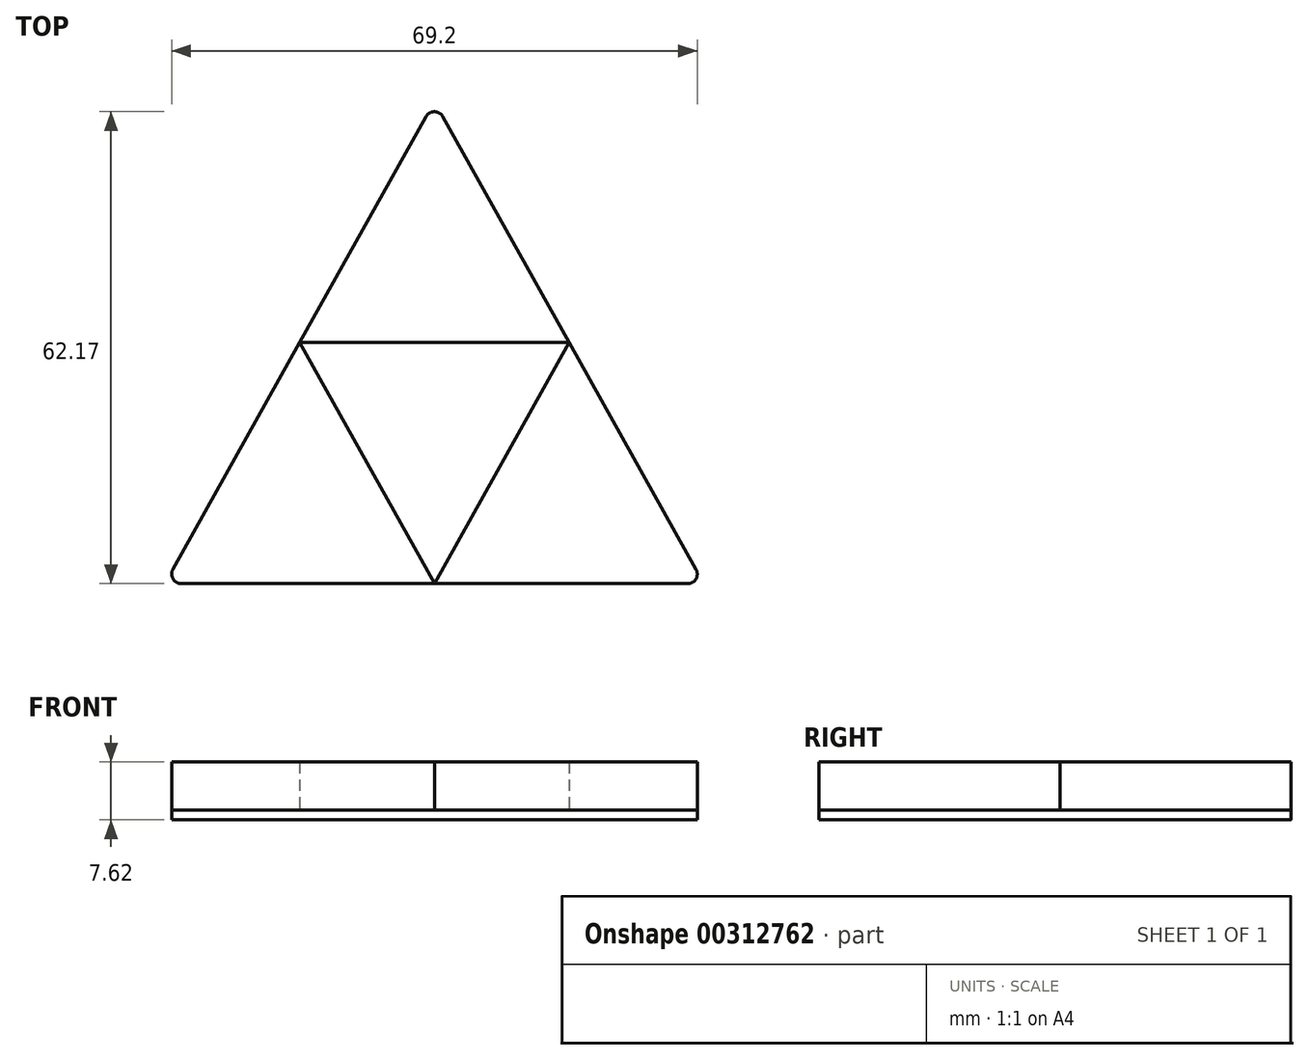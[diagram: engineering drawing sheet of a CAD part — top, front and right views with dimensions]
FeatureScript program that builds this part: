
annotation { "Feature Type Name" : "Feature", "Feature Type Description" : "" }
export const myFeature = defineFeature(function(context is Context, id is Id, definition is map)
    precondition{}
    {
        {
            var Q0;
            Q0=qCreatedBy(makeId("Top.planeOp"),FACE);
            var sketch = newSketch(context, id + "F0", { "sketchPlane" : qUnion([Q0])});
            skLineSegment(sketch, "E0.bottom", {"start": v(35.5, 31.75) * mm, "end": v(-35.5, 31.75) * mm});
            skLineSegment(sketch, "E0.top", {"start": v(35.5, -31.75) * mm, "end": v(-35.5, -31.75) * mm});
            skLineSegment(sketch, "E0.left", {"start": v(35.5, 31.75) * mm, "end": v(35.5, -31.75) * mm});
            skLineSegment(sketch, "E0.right", {"start": v(-35.5, 31.75) * mm, "end": v(-35.5, -31.75) * mm});
            skPoint(sketch, "E0.middle", {"position": v(0, 0) * mm});
            skLineSegment(sketch, "E1", {"start": v(0, 31.75) * mm, "end": v(-35.5, -31.75) * mm});
            skLineSegment(sketch, "E2", {"start": v(-35.5, -31.75) * mm, "end": v(35.5, -31.75) * mm});
            skLineSegment(sketch, "E3", {"start": v(35.5, -31.75) * mm, "end": v(0, 31.75) * mm});
            skSolve(sketch);
        }
        {
            var Q0;
            Q0=makeQuery(id+"F0.imprint","IMPRINT",FACE,{"disambiguationData":[TD([[makeQuery(id+"F0.imprint","IMPRINT",EDGE,{"derivedFrom":sQuery(id+"F0.wireOp",EDGE,"E1")}),1.0]])]});
            extrude(context, id + "F1", {"entities" : qUnion([Q0]), "depth" : 1.27 * mm});
        }
        {
            var Q0;
            Q0=makeQuery(id+"F1.opExtrude","CAP_FACE",FACE,{"disambiguationData":[OSD([sQuery(id+"F0.wireOp",EDGE,"E1"),sQuery(id+"F0.wireOp",EDGE,"E2"),sQuery(id+"F0.wireOp",EDGE,"E3")])],"isStart":false});
            var sketch = newSketch(context, id + "F2", { "sketchPlane" : qUnion([Q0])});
            skLineSegment(sketch, "E4", {"start": v(0, -31.75) * mm, "end": v(-17.75, 0) * mm});
            skLineSegment(sketch, "E5", {"start": v(0, -31.75) * mm, "end": v(17.75, 0) * mm});
            skLineSegment(sketch, "E6", {"start": v(17.75, 0) * mm, "end": v(-17.75, 0) * mm});
            skSolve(sketch);
        }
        {
            var Q0;
            {var subQ0=sQuery(id+"F2.wireOp",EDGE,"E5");Q0=makeQuery(id+"F2.imprint","IMPRINT",FACE,{"disambiguationData":[TD([[makeQuery(id+"F2.imprint","IMPRINT",EDGE,{"derivedFrom":subQ0}),-1.0]])]});}
            var Q1;
            {var subQ0=sQuery(id+"F2.wireOp",EDGE,"E4");Q1=makeQuery(id+"F2.imprint","IMPRINT",FACE,{"disambiguationData":[TD([[makeQuery(id+"F2.imprint","IMPRINT",EDGE,{"derivedFrom":subQ0}),1.0]])]});}
            var Q2;
            {var subQ0=sQuery(id+"F2.wireOp",EDGE,"E6");Q2=makeQuery(id+"F2.imprint","IMPRINT",FACE,{"disambiguationData":[TD([[makeQuery(id+"F2.imprint","IMPRINT",EDGE,{"derivedFrom":subQ0}),-1.0]])]});}
            extrude(context, id + "F3", {"entities" : qUnion([Q0, Q1, Q2]), "depth" : 6.35 * mm});
        }
        {
            var Q0;
            Q0=makeQuery(id+"F3.opExtrude","SWEPT_EDGE",EDGE,{"disambiguationData":[OSD([sQuery(id+"F0.wireOp",EDGE,"E1"),sQuery(id+"F0.wireOp",EDGE,"E2")])]});
            var Q1;
            Q1=makeQuery(id+"F3.opExtrude","SWEPT_EDGE",EDGE,{"disambiguationData":[OSD([sQuery(id+"F0.wireOp",EDGE,"E2"),sQuery(id+"F0.wireOp",EDGE,"E3")])]});
            var Q2;
            Q2=makeQuery(id+"F1.opExtrude","SWEPT_EDGE",EDGE,{"disambiguationData":[OSD([sQuery(id+"F0.wireOp",EDGE,"E0.left"),sQuery(id+"F0.wireOp",EDGE,"E2"),sQuery(id+"F0.wireOp",EDGE,"E3")])]});
            var Q3;
            Q3=makeQuery(id+"F3.opExtrude","SWEPT_EDGE",EDGE,{"disambiguationData":[OSD([sQuery(id+"F0.wireOp",EDGE,"E1"),sQuery(id+"F0.wireOp",EDGE,"E3")])]});
            var Q4;
            Q4=makeQuery(id+"F1.opExtrude","SWEPT_EDGE",EDGE,{"disambiguationData":[OSD([sQuery(id+"F0.wireOp",EDGE,"E0.bottom"),sQuery(id+"F0.wireOp",EDGE,"E1"),sQuery(id+"F0.wireOp",EDGE,"E3")])]});
            var Q5;
            Q5=makeQuery(id+"F1.opExtrude","SWEPT_EDGE",EDGE,{"disambiguationData":[OSD([sQuery(id+"F0.wireOp",EDGE,"E0.right"),sQuery(id+"F0.wireOp",EDGE,"E1"),sQuery(id+"F0.wireOp",EDGE,"E2")])]});
            fillet(context, id + "F4", {"entities" : qUnion([Q0, Q1, Q2, Q3, Q4, Q5]), "radius" : 1.27 * mm, "tangentPropagation" : true, "allowEdgeOverflow" : false});
        }
    });
